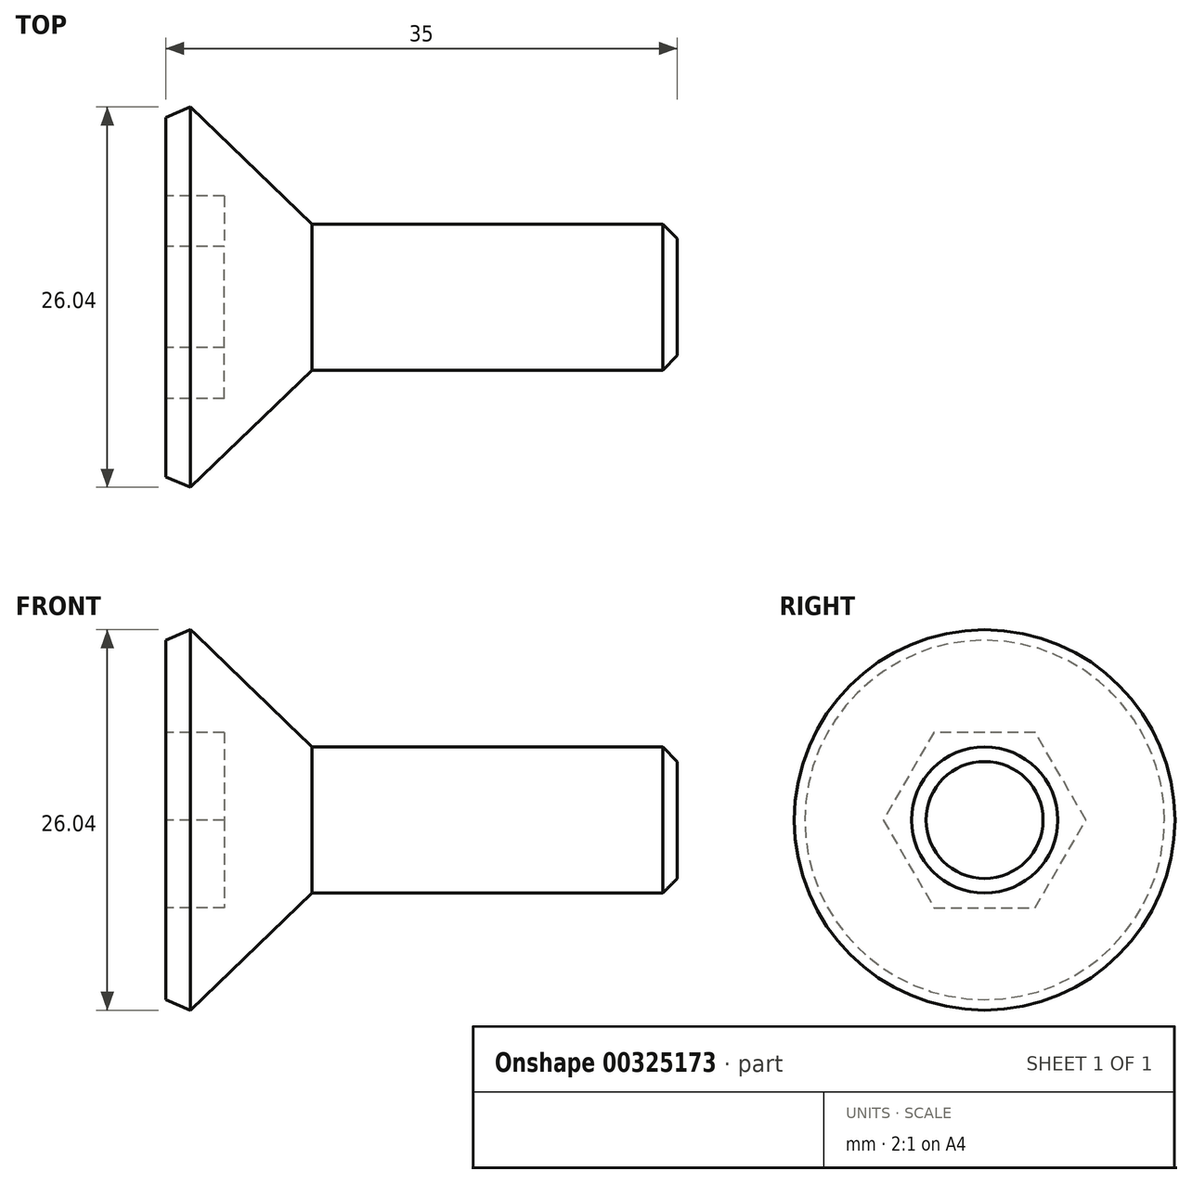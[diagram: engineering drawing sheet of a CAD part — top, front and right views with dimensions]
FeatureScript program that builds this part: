
annotation { "Feature Type Name" : "Feature", "Feature Type Description" : "" }
export const myFeature = defineFeature(function(context is Context, id is Id, definition is map)
    precondition{}
    {
        {
            var Q0;
            Q0=qCreatedBy(makeId("Front.planeOp"),FACE);
            var sketch = newSketch(context, id + "F0", { "sketchPlane" : qUnion([Q0])});
            skLineSegment(sketch, "E0", {"start": v(0, 0) * mm, "end": v(0, 14.66) * mm});
            skLineSegment(sketch, "E1", {"start": v(0, 14.66) * mm, "end": v(10, 5) * mm});
            skLineSegment(sketch, "E2", {"start": v(10, 5) * mm, "end": v(35, 5) * mm});
            skLineSegment(sketch, "E3", {"start": v(35, 5) * mm, "end": v(35, 0) * mm});
            skLineSegment(sketch, "E4", {"start": v(35, 0) * mm, "end": v(0, 0) * mm});
            skLineSegment(sketch, "E5", {"start": v(35, 0) * mm, "end": v(47.86, 0) * mm, "construction": true});
            skSolve(sketch);
        }
        {
            var Q0;
            Q0=makeQuery(id+"F0.imprint","IMPRINT",FACE,{"disambiguationData":[TD([[makeQuery(id+"F0.imprint","IMPRINT",EDGE,{"derivedFrom":sQuery(id+"F0.wireOp",EDGE,"E0")}),-1.0]])]});
            var Q1;
            Q1=sQuery(id+"F0.wireOp",EDGE,"E5");
            revolve(context, id + "F1", {"entities" : qUnion([Q0]), "axis" : qUnion([Q1]), "revolveType" : RevolveType.FULL});
        }
        {
            var Q0;
            Q0=makeQuery(id+"F1.opRevolve","SWEPT_FACE",FACE,{"disambiguationData":[OSD([sQuery(id+"F0.wireOp",EDGE,"E0")])]});
            var sketch = newSketch(context, id + "F2", { "sketchPlane" : qUnion([Q0])});
            skCircle(sketch, "E6.cCircle", {"center": v(0, 0) * mm, "radius": 6 * mm, "construction": true});
            skLineSegment(sketch, "E6.0", {"start": v(3.46, -6) * mm, "end": v(-3.46, -6) * mm});
            skLineSegment(sketch, "E6.1", {"start": v(-3.46, -6) * mm, "end": v(-6.93, 0) * mm});
            skLineSegment(sketch, "E6.2", {"start": v(-6.93, 0) * mm, "end": v(-3.46, 6) * mm});
            skLineSegment(sketch, "E6.3", {"start": v(-3.46, 6) * mm, "end": v(3.46, 6) * mm});
            skLineSegment(sketch, "E6.4", {"start": v(3.46, 6) * mm, "end": v(6.93, 0) * mm});
            skLineSegment(sketch, "E6.5", {"start": v(6.93, 0) * mm, "end": v(3.46, -6) * mm});
            skPoint(sketch, "E6.0.midPoint", {"position": v(0, -6) * mm});
            skSolve(sketch);
        }
        {
            var Q0;
            Q0=makeQuery(id+"F2.imprint","IMPRINT",FACE,{"disambiguationData":[TD([[makeQuery(id+"F2.imprint","IMPRINT",EDGE,{"derivedFrom":sQuery(id+"F2.wireOp",EDGE,"E6.0")}),-1.0]])]});
            extrude(context, id + "F3", {"entities" : qUnion([Q0]), "operationType" : NewBodyOperationType.REMOVE, "oppositeDirection" : true, "depth" : 4 * mm});
        }
        {
            var Q0;
            Q0=makeQuery(id+"F1.opRevolve","SWEPT_FACE",FACE,{"disambiguationData":[OSD([sQuery(id+"F0.wireOp",EDGE,"E3")])]});
            chamfer(context, id + "F4", {"entities" : qUnion([Q0]), "width" : 1 * mm, "tangentPropagation" : true});
        }
        {
            var Q0;
            Q0=makeQuery(id+"F1.opRevolve","SWEPT_EDGE",EDGE,{"disambiguationData":[OSD([sQuery(id+"F0.wireOp",EDGE,"E0"),sQuery(id+"F0.wireOp",EDGE,"E1")])]});
            chamfer(context, id + "F5", {"entities" : qUnion([Q0]), "width" : 1 * mm, "tangentPropagation" : true});
        }
    });
